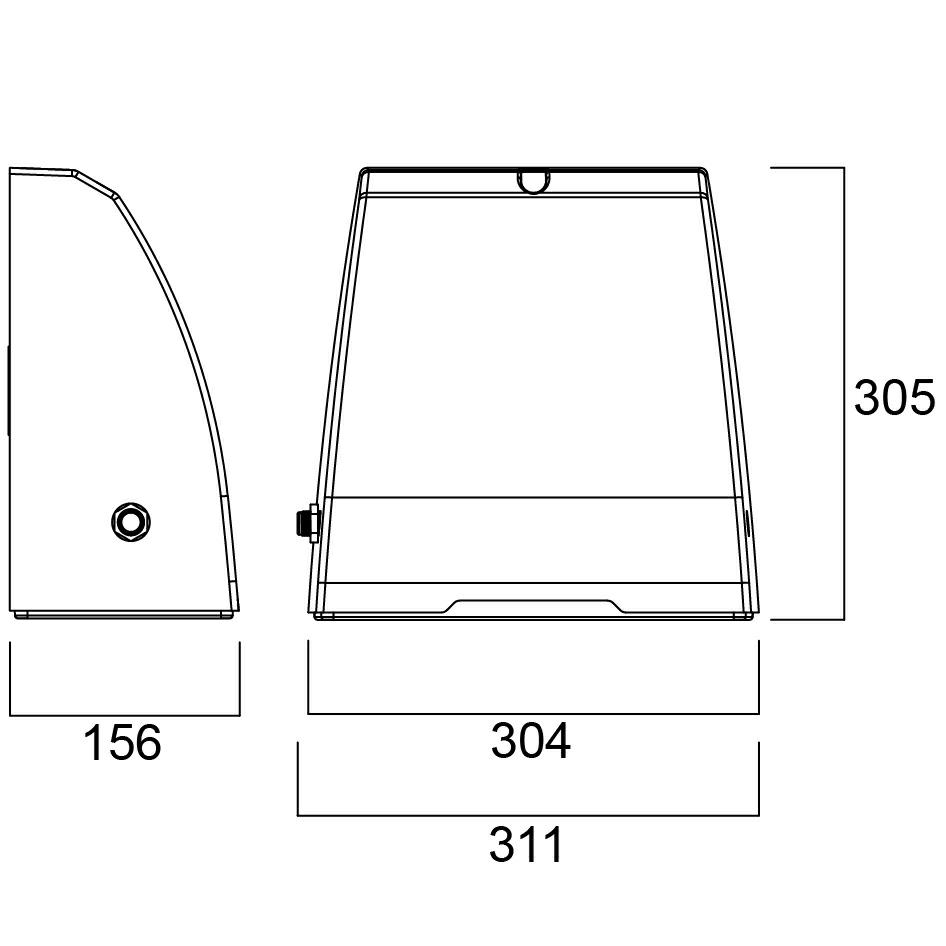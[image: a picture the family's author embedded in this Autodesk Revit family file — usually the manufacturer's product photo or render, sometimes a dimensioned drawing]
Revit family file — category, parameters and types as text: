
# Revit family: 0049944_1700lm
name_source: partatom
category: Lighting Fixtures
revit_build: Autodesk Revit 2018 (Build: 20170223_1515(x64)
units: mm (PartAtom-declared; Revit-internal decimal feet)

## family parameters
Cut with Voids When Loaded = No
Host = Face
Light Source = Yes
OmniClass Number = 23.80.70.00
OmniClass Title = Lighting
Part Type = Normal
Room Calculation Point = No
Round Connector Dimension = Use Diameter
Shared = No

## types (1)
- 0049944 MURO SURF IP65 1700-3250LM 840 PH GR
    Apparent Load = 28 VA
    Assembly Code = D5020200
    AssetType = Fixed
    ClassificationName = Uniclass2015
    ClassificationValue = EF_70_80
    Color Filter = 16777215
    Cost = 0 $
    Default Elevation = 1219 mm
    Description = Muro Surface is a wall mounted fixture for exterior lighting applications. Comes with aluminium housing in RAL7016 anthracite grey colour, frosted PC diffuser, IP65, IK10, Class I, 4000K, non-dimmable multipower driver with 5 settings, 1700 / 1900 / 2750 / 3150 / 3250 lm, 14 / 16 / 24 / 27 / 28 W, up to 121 lm/W total system efficacy, switchable built in Mini photocell, CRI80, Asymmetrical beam, 119.000 hrs L70B50 lifespan, 304 x 305 x 155 mm (L x W x D) dimensions, 4.1 kg weight.
    Dimming Lamp Color Temperature Shift = <None>
    DocumentationLiterature = http://www.sylvania-lighting.com
    ElectricShockClassification = 116
    Emit Shape Visible in Rendering = No
    Emit from Circle Diameter = 610 mm
    IfcExportAs = Class I
    IfcExportType = IfcLightFixtureType
    ImpactProtectionIndex = IfcLightFixtureType
    IngressProtection = IfcLightFixtureType
    InputNominalFrequency = 4000
    InputVoltage = 0
    LampColourRenderingIndex = 16500
    LampColourTemperature = LED
    LampMacAdamStep = 80
    LampNominalLuminous = 4000 K
    LightOutputRatio = LED
    LuminaireType = 0
    ManufacturerName = 116 lm/W
    Material = Feilo Sylvania
    Material_1_SYL = <By Category>
    Material_2_SYL = <By Category>
    Material_3_SYL = <By Category>
    Material_4_SYL = <By Category>
    Model = Muro Surface IP65 1700-3250lm 840 PH Grey
    ModelNumber = 0049944
    ModelReference = Muro Surface IP65 1700-3250lm 840 PH Grey
    Name = Muro Surface IP65 1700-3250lm 840 PH Grey
    NominalDepth = 155 mm  [stored 0.50853 ft]
    NominalHeight = 305 mm  [stored 1.00066 ft]
    NominalLength = 155 mm  [stored 0.50853 ft]
    Photometric Web File = 0049944_1700lm.IES
    PowerConsumption = Lighting
    PowerFactor = 0.95
    Tilt Angle = -90.00°
    Type Image = <None>
    TypeName = Muro Surface IP65 1700-3250lm 840 PH Grey
    URL = 0.9
    Voltage = 0 V
    WarrantyDescription = http://www.sylvania-lighting.com

note: [stored X ft] marks values corroborated as IEEE doubles in the binary element streams (Revit-internal decimal feet)

## geometry (parser evidence)
native form markers: Sweep x1
no freeform markers — native parametric forms only
